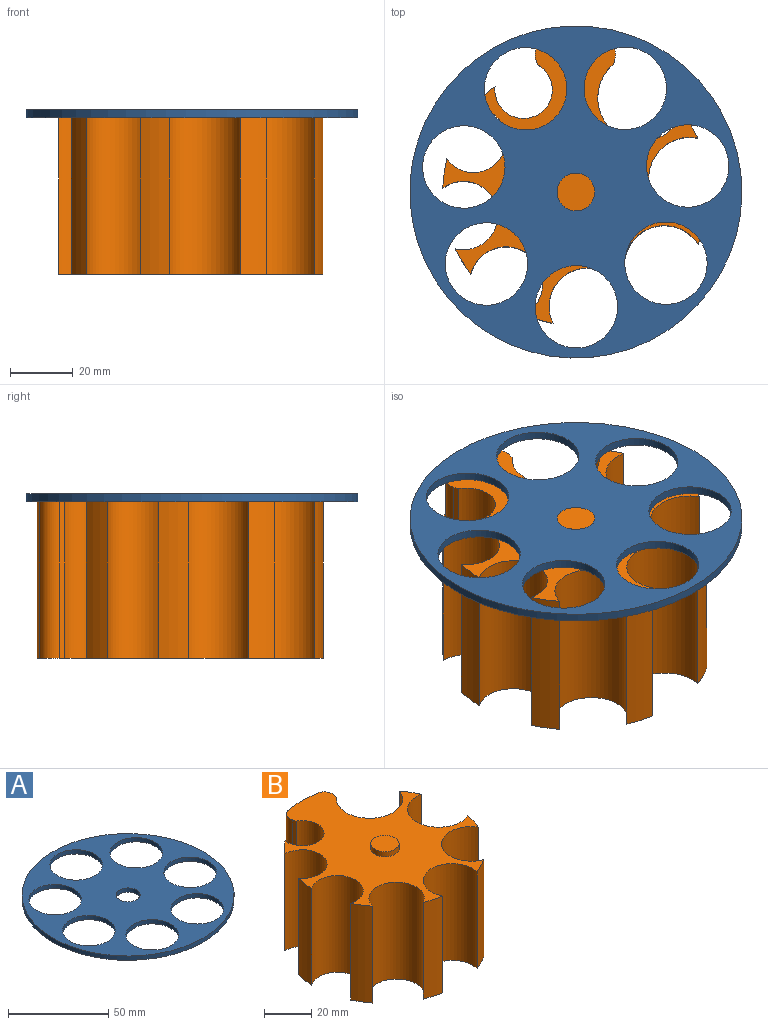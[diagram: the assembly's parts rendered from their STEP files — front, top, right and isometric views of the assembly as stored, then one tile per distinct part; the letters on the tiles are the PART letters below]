
ASSEMBLY  parts=2 mates=1
PART A: 11 faces, bbox 106x106x2.6 mm
  f0: cylinder r=53mm len=106mm, axis (0,0,-1), area 865.8mm2, adj f9,f10
  f1: cylinder r=13.15mm len=26.3mm, axis (0,0,-1), area 214.8mm2, adj f9,f10
  f2: cylinder r=13.15mm len=26.3mm, axis (0,0,-1), area 214.8mm2, adj f9,f10
  f3: cylinder r=13.15mm len=26.3mm, axis (0,0,-1), area 214.8mm2, adj f9,f10
  f4: cylinder r=13.15mm len=26.3mm, axis (0,0,-1), area 214.8mm2, adj f9,f10
  f5: cylinder r=13.15mm len=26.3mm, axis (0,0,-1), area 214.8mm2, adj f9,f10
  f6: cylinder r=13.15mm len=26.3mm, axis (0,0,-1), area 214.8mm2, adj f9,f10
  f7: cylinder r=13.15mm len=26.3mm, axis (0,0,-1), area 214.8mm2, adj f9,f10
  f8: cylinder r=6mm len=12mm, axis (0,0,-1), area 98mm2, adj f9,f10
  f9: plane 106x106mm, normal (0,0,1), area 4908.9mm2, adj f0,f1,f2,f3,f4,f5,f6,f7
  f10: plane 106x106mm, normal (0,0,-1), area 4908.9mm2, adj f0,f1,f2,f3,f4,f5,f6,f7
PART B: 24 faces, bbox 84.3x91.4x52.6 mm
  f0: cylinder r=13.93mm len=50mm, axis (0,0,-1), area 2558.9mm2, adj f14,f15,f16,f19
  f1: cylinder r=9.18mm len=50mm, axis (0,0,-1), area 1990.3mm2, adj f2,f15,f16,f20
  f2: cylinder r=42.5mm len=50mm, axis (0,0,-1), area 485.5mm2, adj f1,f3,f15,f16
  f3: cylinder r=10.43mm len=50mm, axis (0,0,-1), area 2140.3mm2, adj f2,f4,f15,f16
  f4: cylinder r=42.5mm len=50mm, axis (0,0,-1), area 475.7mm2, adj f3,f5,f15,f16
  f5: cylinder r=10.93mm len=50mm, axis (0,0,-1), area 2200.7mm2, adj f4,f6,f15,f16
  f6: cylinder r=42.5mm len=50mm, axis (0,0,-1), area 472.9mm2, adj f5,f7,f15,f16
  f7: cylinder r=11.67mm len=50mm, axis (0,0,-1), area 2291.3mm2, adj f6,f8,f15,f16
  f8: cylinder r=42.5mm len=50mm, axis (0,0,-1), area 471.7mm2, adj f7,f9,f15,f16
  f9: cylinder r=12.18mm len=50mm, axis (0,0,-1), area 2351.4mm2, adj f8,f10,f15,f16
  f10: cylinder r=42.5mm len=50mm, axis (0,0,-1), area 472.3mm2, adj f9,f11,f15,f16
  f11: cylinder r=12.68mm len=50mm, axis (0,0,-1), area 2411.2mm2, adj f10,f12,f15,f16
  f12: cylinder r=42.5mm len=50mm, axis (0,0,-1), area 473.8mm2, adj f11,f13,f15,f16
  f13: cylinder r=13.17mm len=50mm, axis (0,0,-1), area 2470.6mm2, adj f12,f14,f15,f16
  f14: cylinder r=42.5mm len=50mm, axis (0,0,-1), area 477.1mm2, adj f0,f13,f15,f16
  f15: plane 91.37x84.27mm, normal (0,0,1), area 2994.9mm2, adj f0,f1,f2,f3,f4,f5,f6,f7
  f16: plane 91.37x84.27mm, normal (0,0,-1), area 3108mm2, adj f0,f1,f2,f3,f4,f5,f6,f7
  f17: cylinder r=6mm len=12mm, axis (0,0,-1), area 98mm2, adj f15,f18
  f18: plane 12x12mm, normal (0,0,1), area 113.1mm2, adj f17
  f19: plane 50x1.65mm, normal (0.96,-0.28,0), area 85.9mm2, adj f0,f15,f16,f22
  f20: plane 50x1.64mm, normal (-0.96,-0.29,0), area 85.9mm2, adj f1,f15,f16,f23
  f21: cylinder r=49.5mm len=50mm, axis (0,0,-1), area 877.3mm2, adj f15,f16,f22,f23
  f22: cylinder r=5mm len=50mm, axis (0,0,-1), area 420.8mm2, adj f15,f16,f19,f21
  f23: cylinder r=5mm len=50mm, axis (0,0,-1), area 420.8mm2, adj f15,f16,f20,f21
PLACE A rot(axis=(0,0,1),77.4deg) t=(-8.15,29.02,-0.72)mm
PLACE B t=(-8.15,29.02,-0.72)mm fixed
MATE revolute B.f17 <-> A.f8  axis (0,0,1) through (-8.15,29.02,49.28)mm
